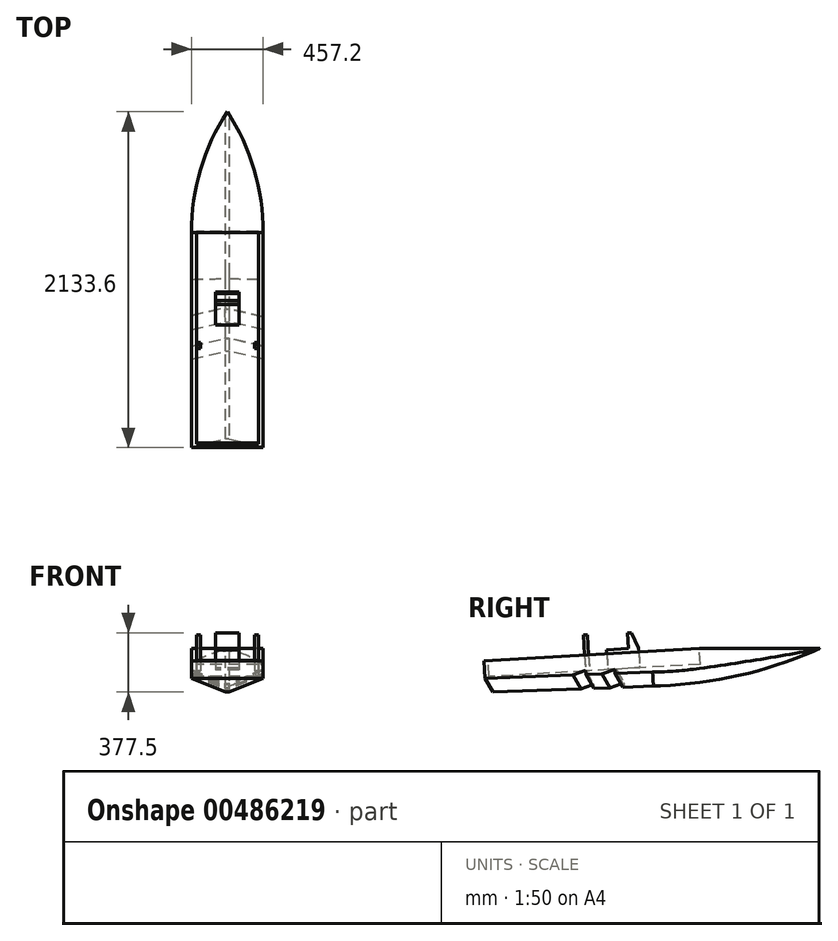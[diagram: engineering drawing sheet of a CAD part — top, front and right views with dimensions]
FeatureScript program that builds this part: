
annotation { "Feature Type Name" : "Feature", "Feature Type Description" : "" }
export const myFeature = defineFeature(function(context is Context, id is Id, definition is map)
    precondition{}
    {
        {
            var Q0;
            Q0=qCreatedBy(makeId("Right.planeOp"),FACE);
            var sketch = newSketch(context, id + "F0", { "sketchPlane" : qUnion([Q0])});
            skLineSegment(sketch, "E0", {"start": v(-869.62, -245.55) * mm, "end": v(497.03, -166) * mm});
            skLineSegment(sketch, "E1", {"start": v(-869.62, -245.55) * mm, "end": v(-863.13, -357.05) * mm});
            skLineSegment(sketch, "E2", {"start": v(-863.13, -357.05) * mm, "end": v(250.24, -314.95) * mm});
            skLineSegment(sketch, "E3", {"start": v(497.03, -166) * mm, "end": v(1263.98, -166) * mm});
            skArc(sketch, "E4", {"start": v(250.24, -314.95) * mm, "mid": v(761.14, -267.9) * mm, "end": v(1263.98, -166) * mm});
            skLineSegment(sketch, "E5", {"start": v(-857.96, -445.8) * mm, "end": v(250.24, -403.9) * mm});
            skArc(sketch, "E6", {"start": v(250.24, -403.9) * mm, "mid": v(768.61, -333.94) * mm, "end": v(1263.98, -166) * mm});
            skLineSegment(sketch, "E7", {"start": v(-863.13, -357.05) * mm, "end": v(-812.8, -444.09) * mm});
            skSolve(sketch);
        }
        {
            var Q0;
            Q0=makeQuery(id+"F0.imprint","IMPRINT",FACE,{"disambiguationData":[TD([[makeQuery(id+"F0.imprint","IMPRINT",EDGE,{"derivedFrom":sQuery(id+"F0.wireOp",EDGE,"E0")}),-1.0]])]});
            var Q1;
            Q1=makeQuery(id+"F0.imprint","IMPRINT",FACE,{"disambiguationData":[TD([[makeQuery(id+"F0.imprint","IMPRINT",EDGE,{"derivedFrom":sQuery(id+"F0.wireOp",EDGE,"E2")}),-1.0]])]});
            extrude(context, id + "F1", {"entities" : qUnion([Q0, Q1]), "depth" : 457.2 * mm, "offsetDistance" : 25.4 * mm});
        }
        {
            var Q0;
            Q0=makeQuery(id+"F1.opExtrude","SWEPT_FACE",FACE,{"disambiguationData":[OSD([sQuery(id+"F0.wireOp",EDGE,"E1")])]});
            var sketch = newSketch(context, id + "F2", { "sketchPlane" : qUnion([Q0])});
            skLineSegment(sketch, "E8", {"start": v(0, -306.29) * mm, "end": v(228.6, -399.45) * mm});
            skPoint(sketch, "E8.endSnap0", {"position": v(228.6, -306.29) * mm});
            skLineSegment(sketch, "E9", {"start": v(228.6, -399.45) * mm, "end": v(457.2, -306.29) * mm});
            skLineSegment(sketch, "E10", {"start": v(457.2, -306.29) * mm, "end": v(500.55, -412.66) * mm});
            skLineSegment(sketch, "E11", {"start": v(500.55, -412.66) * mm, "end": v(-44.86, -412.66) * mm});
            skLineSegment(sketch, "E12", {"start": v(-44.86, -412.66) * mm, "end": v(0, -306.29) * mm});
            skSolve(sketch);
        }
        {
            var Q0;
            Q0=makeQuery(id+"F2.imprint","IMPRINT",FACE,{"disambiguationData":[TD([[makeQuery(id+"F2.imprint","IMPRINT",EDGE,{"derivedFrom":sQuery(id+"F2.wireOp",EDGE,"E8")}),-1.0]])]});
            var Q1;
            Q1=makeQuery(id+"F1.opExtrude","CAP_EDGE",EDGE,{"disambiguationData":[OSD([sQuery(id+"F0.wireOp",EDGE,"E5")])],"isStart":false});
            var Q2;
            Q2=makeQuery(id+"F1.opExtrude","CAP_EDGE",EDGE,{"disambiguationData":[OSD([sQuery(id+"F0.wireOp",EDGE,"E6")])],"isStart":false});
            sweep(context, id + "F3", {"operationType" : NewBodyOperationType.REMOVE, "profiles" : qUnion([Q0]), "path" : qUnion([Q1, Q2])});
        }
        {
            var Q0;
            Q0=makeQuery(id+"F1.opExtrude","SWEPT_FACE",FACE,{"disambiguationData":[OSD([sQuery(id+"F0.wireOp",EDGE,"E3")])]});
            var sketch = newSketch(context, id + "F4", { "sketchPlane" : qUnion([Q0])});
            skPoint(sketch, "E13.startSnap0", {"position": v(228.6, 1263.98) * mm});
            skLineSegment(sketch, "E14", {"start": v(228.6, 1204.03) * mm, "end": v(228.6, 1037.29) * mm, "construction": true});
            skLineSegment(sketch, "E15", {"start": v(0, 497.03) * mm, "end": v(-662.43, 1118.52) * mm});
            skLineSegment(sketch, "E16", {"start": v(-662.43, 1118.52) * mm, "end": v(-136.56, 1315.19) * mm});
            skLineSegment(sketch, "E17", {"start": v(-136.56, 1315.19) * mm, "end": v(782.16, 1315.19) * mm});
            skLineSegment(sketch, "E18", {"start": v(782.16, 1315.19) * mm, "end": v(457.2, 497.03) * mm});
            skArc(sketch, "E19", {"start": v(228.6, 1263.98) * mm, "mid": v(58.37, 897.18) * mm, "end": v(0, 497.03) * mm});
            skArc(sketch, "E20.MirrorCS", {"start": v(228.6, 1263.98) * mm, "mid": v(398.83, 897.18) * mm, "end": v(457.2, 497.03) * mm});
            skSolve(sketch);
        }
        {
            var Q0;
            Q0 = qSketchRegion(id + "F4", true);
            extrude(context, id + "F5", {"entities" : qUnion([Q0]), "operationType" : NewBodyOperationType.REMOVE, "oppositeDirection" : true, "depth" : 584.2 * mm, "offsetDistance" : 25.4 * mm});
        }
        {
            var Q0;
            {var subQ0=sQuery(id+"F0.wireOp",EDGE,"E7");var subQ1=sQuery(id+"F0.wireOp",EDGE,"E3");var subQ2=sQuery(id+"F0.wireOp",EDGE,"E1");var subQ4=sQuery(id+"F0.wireOp",EDGE,"E5");var subQ5=sQuery(id+"F0.wireOp",EDGE,"E0");var subQ6=sQuery(id+"F0.wireOp",EDGE,"E6");Q0=makeQuery(id+"F3.boolean.opBoolean","SPLIT",FACE,{"disambiguationData":[TD([makeQuery(id+"F1.opExtrude","SWEPT_FACE",FACE,{"disambiguationData":[OSD([subQ5])]})])],"derivedFrom":makeQuery(id+"F1.opExtrude","CAP_FACE",FACE,{"disambiguationData":[OSD([subQ5,subQ2,subQ1,subQ4,subQ6,subQ0])],"isStart":true})});}
            var sketch = newSketch(context, id + "F6", { "sketchPlane" : qUnion([Q0])});
            skLineSegment(sketch, "E21", {"start": v(28, -325.47) * mm, "end": v(28.95, -300.1) * mm});
            skLineSegment(sketch, "E22", {"start": v(28.95, -300.1) * mm, "end": v(120.28, -328.96) * mm});
            skLineSegment(sketch, "E23", {"start": v(120.28, -328.96) * mm, "end": v(28, -325.47) * mm});
            skLineSegment(sketch, "E24", {"start": v(224.19, -332.9) * mm, "end": v(224.19, -307.5) * mm});
            skLineSegment(sketch, "E25", {"start": v(224.19, -307.5) * mm, "end": v(306.2, -336) * mm});
            skLineSegment(sketch, "E26", {"start": v(306.2, -336) * mm, "end": v(863.13, -357.05) * mm, "construction": true});
            skSolve(sketch);
        }
        {
            var Q0;
            Q0=makeQuery(id+"F6.imprint","IMPRINT",FACE,{"disambiguationData":[TD([[makeQuery(id+"F6.imprint","IMPRINT",EDGE,{"derivedFrom":sQuery(id+"F6.wireOp",EDGE,"E21")}),-1.0]])]});
            var Q1;
            {var subQ0=sQuery(id+"F6.wireOp",EDGE,"E24");Q1=makeQuery(id+"F6.imprint","IMPRINT",FACE,{"disambiguationData":[TD([[makeQuery(id+"F6.imprint","IMPRINT",EDGE,{"derivedFrom":subQ0}),-1.0]])]});}
            var Q2;
            Q2=makeQuery(id+"F3.boolean.opBoolean","INTERSECT",EDGE,{"derivedFrom":[makeQuery(id+"F1.opExtrude","SWEPT_FACE",FACE,{"disambiguationData":[OSD([sQuery(id+"F0.wireOp",EDGE,"E7")])]}),makeQuery(id+"F3.opSweep","SWEPT_FACE",FACE,{"disambiguationData":[OSD([sQuery(id+"F0.wireOp",EDGE,"E5"),sQuery(id+"F2.wireOp",EDGE,"E8")])]})]});
            sweep(context, id + "F7", {"operationType" : NewBodyOperationType.REMOVE, "profiles" : qUnion([Q0, Q1]), "path" : qUnion([Q2])});
        }
        {
            var Q0;
            {var subQ0=sQuery(id+"F0.wireOp",EDGE,"E7");var subQ1=sQuery(id+"F0.wireOp",EDGE,"E3");var subQ3=sQuery(id+"F0.wireOp",EDGE,"E5");var subQ4=sQuery(id+"F0.wireOp",EDGE,"E1");var subQ5=sQuery(id+"F0.wireOp",EDGE,"E0");var subQ6=sQuery(id+"F0.wireOp",EDGE,"E6");Q0=makeQuery(id+"F3.boolean.opBoolean","SPLIT",FACE,{"disambiguationData":[TD([makeQuery(id+"F1.opExtrude","SWEPT_FACE",FACE,{"disambiguationData":[OSD([subQ5])]})])],"derivedFrom":makeQuery(id+"F1.opExtrude","CAP_FACE",FACE,{"disambiguationData":[OSD([subQ5,subQ4,subQ1,subQ3,subQ6,subQ0])],"isStart":false})});}
            var sketch = newSketch(context, id + "F8", { "sketchPlane" : qUnion([Q0])});
            skLineSegment(sketch, "E27", {"start": v(-863.13, -357.05) * mm, "end": v(-306.2, -336) * mm, "construction": true});
            skLineSegment(sketch, "E28", {"start": v(-306.2, -336) * mm, "end": v(-224.19, -332.9) * mm, "construction": true});
            skLineSegment(sketch, "E29", {"start": v(-224.19, -332.9) * mm, "end": v(-225.66, -307.53) * mm});
            skLineSegment(sketch, "E30", {"start": v(-225.66, -307.53) * mm, "end": v(-306.2, -336) * mm});
            skLineSegment(sketch, "E31", {"start": v(-224.19, -332.9) * mm, "end": v(-120.28, -328.96) * mm, "construction": true});
            skLineSegment(sketch, "E32", {"start": v(-120.28, -328.96) * mm, "end": v(-38.27, -325.86) * mm, "construction": true});
            skLineSegment(sketch, "E33", {"start": v(-38.27, -325.86) * mm, "end": v(-39.74, -300.5) * mm});
            skLineSegment(sketch, "E34", {"start": v(-39.74, -300.5) * mm, "end": v(-120.28, -328.96) * mm});
            skSolve(sketch);
        }
        {
            var Q0;
            {var subQ0=sQuery(id+"F8.wireOp",EDGE,"E29");Q0=makeQuery(id+"F8.imprint","IMPRINT",FACE,{"disambiguationData":[TD([[makeQuery(id+"F8.imprint","IMPRINT",EDGE,{"derivedFrom":subQ0}),1.0]])]});}
            var Q1;
            {var subQ0=sQuery(id+"F8.wireOp",EDGE,"E33");Q1=makeQuery(id+"F8.imprint","IMPRINT",FACE,{"disambiguationData":[TD([[makeQuery(id+"F8.imprint","IMPRINT",EDGE,{"derivedFrom":subQ0}),1.0]])]});}
            var Q2;
            Q2=makeQuery(id+"F3.boolean.opBoolean","INTERSECT",EDGE,{"derivedFrom":[makeQuery(id+"F1.opExtrude","SWEPT_FACE",FACE,{"disambiguationData":[OSD([sQuery(id+"F0.wireOp",EDGE,"E7")])]}),makeQuery(id+"F3.opSweep","SWEPT_FACE",FACE,{"disambiguationData":[OSD([sQuery(id+"F0.wireOp",EDGE,"E5"),sQuery(id+"F2.wireOp",EDGE,"E9")])]})]});
            sweep(context, id + "F9", {"operationType" : NewBodyOperationType.REMOVE, "profiles" : qUnion([Q0, Q1]), "path" : qUnion([Q2])});
        }
        {
            var Q0;
            Q0=makeQuery(id+"F9.boolean.opBoolean","COPY",FACE,{"derivedFrom":makeQuery(id+"F9.opSweep","CAP_FACE",FACE,{"disambiguationData":[OSD([sQuery(id+"F0.wireOp",EDGE,"E1"),sQuery(id+"F0.wireOp",EDGE,"E2"),sQuery(id+"F0.wireOp",EDGE,"E5"),sQuery(id+"F0.wireOp",EDGE,"E7"),sQuery(id+"F2.wireOp",EDGE,"E9"),sQuery(id+"F2.wireOp",EDGE,"E10"),sQuery(id+"F8.wireOp",EDGE,"E29"),sQuery(id+"F8.wireOp",EDGE,"E30")])],"isStart":false})});
            var sketch = newSketch(context, id + "F10", { "sketchPlane" : qUnion([Q0])});
            skLineSegment(sketch, "E35", {"start": v(-255.86, -423.03) * mm, "end": v(-175.33, -394.58) * mm});
            skLineSegment(sketch, "E36", {"start": v(-175.33, -394.58) * mm, "end": v(-173.86, -419.93) * mm});
            skLineSegment(sketch, "E37", {"start": v(-173.86, -419.93) * mm, "end": v(-255.86, -423.03) * mm});
            skSolve(sketch);
        }
        {
            var Q0;
            Q0 = qSketchRegion(id + "F10", true);
            extrude(context, id + "F11", {"entities" : qUnion([Q0]), "operationType" : NewBodyOperationType.REMOVE, "oppositeDirection" : true, "depth" : 25.4 * mm, "offsetDistance" : 25.4 * mm});
        }
        {
            var Q0;
            Q0=makeQuery(id+"F9.boolean.opBoolean","COPY",FACE,{"derivedFrom":makeQuery(id+"F9.opSweep","CAP_FACE",FACE,{"disambiguationData":[OSD([sQuery(id+"F0.wireOp",EDGE,"E1"),sQuery(id+"F0.wireOp",EDGE,"E2"),sQuery(id+"F0.wireOp",EDGE,"E5"),sQuery(id+"F0.wireOp",EDGE,"E7"),sQuery(id+"F2.wireOp",EDGE,"E9"),sQuery(id+"F2.wireOp",EDGE,"E10"),sQuery(id+"F8.wireOp",EDGE,"E33"),sQuery(id+"F8.wireOp",EDGE,"E34")])],"isStart":false})});
            var sketch = newSketch(context, id + "F12", { "sketchPlane" : qUnion([Q0])});
            skLineSegment(sketch, "E38", {"start": v(-69.94, -416) * mm, "end": v(10.59, -387.55) * mm});
            skLineSegment(sketch, "E39", {"start": v(10.59, -387.55) * mm, "end": v(12.07, -412.9) * mm});
            skLineSegment(sketch, "E40", {"start": v(12.07, -412.9) * mm, "end": v(-69.94, -416) * mm});
            skSolve(sketch);
        }
        {
            var Q0;
            Q0 = qSketchRegion(id + "F12", true);
            extrude(context, id + "F13", {"entities" : qUnion([Q0]), "operationType" : NewBodyOperationType.REMOVE, "oppositeDirection" : true, "depth" : 25.4 * mm, "offsetDistance" : 25.4 * mm});
        }
        {
            var Q0;
            Q0=makeQuery(id+"F1.opExtrude","SWEPT_FACE",FACE,{"disambiguationData":[OSD([sQuery(id+"F0.wireOp",EDGE,"E0")])]});
            var sketch = newSketch(context, id + "F14", { "sketchPlane" : qUnion([Q0])});
            skLineSegment(sketch, "E41", {"start": v(0, 486.54) * mm, "end": v(6.35, 486.54) * mm, "construction": true});
            skLineSegment(sketch, "E42", {"start": v(6.35, 486.54) * mm, "end": v(31.75, 486.54) * mm, "construction": true});
            skLineSegment(sketch, "E43", {"start": v(31.75, 486.54) * mm, "end": v(31.75, -882.42) * mm});
            skPoint(sketch, "E43.endSnap0", {"position": v(228.6, -882.42) * mm});
            skLineSegment(sketch, "E44", {"start": v(228.6, 486.54) * mm, "end": v(228.6, 92.47) * mm, "construction": true});
            skLineSegment(sketch, "E45.MirrorCS", {"start": v(425.45, 486.54) * mm, "end": v(425.45, -882.42) * mm});
            skLineSegment(sketch, "E46", {"start": v(228.6, -882.42) * mm, "end": v(228.6, -857.02) * mm, "construction": true});
            skLineSegment(sketch, "E47", {"start": v(228.6, -857.02) * mm, "end": v(425.45, -857.02) * mm});
            skLineSegment(sketch, "E48", {"start": v(425.45, -857.02) * mm, "end": v(31.75, -857.02) * mm});
            skSolve(sketch);
        }
        {
            var Q0;
            {var subQ0=sQuery(id+"F14.wireOp",EDGE,"E47");Q0=makeQuery(id+"F14.imprint","IMPRINT",FACE,{"disambiguationData":[TD([[makeQuery(id+"F14.imprint","IMPRINT",EDGE,{"derivedFrom":subQ0}),1.0]])]});}
            extrude(context, id + "F15", {"entities" : qUnion([Q0]), "operationType" : NewBodyOperationType.REMOVE, "oppositeDirection" : true, "depth" : 101.6 * mm, "offsetDistance" : 25.4 * mm});
        }
        {
            var Q0;
            Q0=makeQuery(id+"F15.boolean.opBoolean","COPY",FACE,{"derivedFrom":makeQuery(id+"F15.opExtrude","CAP_FACE",FACE,{"disambiguationData":[OSD([sQuery(id+"F0.wireOp",EDGE,"E0"),sQuery(id+"F0.wireOp",EDGE,"E3"),sQuery(id+"F14.wireOp",EDGE,"E43"),sQuery(id+"F14.wireOp",EDGE,"E45.MirrorCS"),sQuery(id+"F14.wireOp",EDGE,"E47"),sQuery(id+"F14.wireOp",EDGE,"E48")])],"isStart":false})});
            var sketch = newSketch(context, id + "F16", { "sketchPlane" : qUnion([Q0])});
            skLineSegment(sketch, "E49", {"start": v(228.6, 486.54) * mm, "end": v(228.6, -857.02) * mm, "construction": true});
            skLineSegment(sketch, "E50.bottom", {"start": v(304.8, 101.6) * mm, "end": v(152.4, 101.6) * mm});
            skLineSegment(sketch, "E50.top", {"start": v(304.8, -101.6) * mm, "end": v(152.4, -101.6) * mm});
            skLineSegment(sketch, "E50.left", {"start": v(304.8, 101.6) * mm, "end": v(304.8, -101.6) * mm});
            skLineSegment(sketch, "E50.right", {"start": v(152.4, 101.6) * mm, "end": v(152.4, -101.6) * mm});
            skPoint(sketch, "E50.middle", {"position": v(228.6, 0) * mm});
            skLineSegment(sketch, "E51", {"start": v(31.75, -218.44) * mm, "end": v(57.15, -218.44) * mm});
            skLineSegment(sketch, "E52", {"start": v(57.15, -218.44) * mm, "end": v(57.15, -243.84) * mm});
            skLineSegment(sketch, "E53", {"start": v(57.15, -243.84) * mm, "end": v(31.75, -243.84) * mm});
            skLineSegment(sketch, "E54", {"start": v(31.75, -243.84) * mm, "end": v(57.15, -231.14) * mm, "construction": true});
            skLineSegment(sketch, "E55.MirrorCS", {"start": v(425.45, -218.44) * mm, "end": v(400.05, -218.44) * mm});
            skLineSegment(sketch, "E56.MirrorCS", {"start": v(400.05, -243.84) * mm, "end": v(425.45, -243.84) * mm});
            skLineSegment(sketch, "E57.MirrorCS", {"start": v(400.05, -218.44) * mm, "end": v(400.05, -243.84) * mm});
            skLineSegment(sketch, "E58", {"start": v(31.75, -218.44) * mm, "end": v(31.75, -243.84) * mm});
            skLineSegment(sketch, "E59", {"start": v(434.33, -218.44) * mm, "end": v(425.45, -218.44) * mm});
            skLineSegment(sketch, "E60", {"start": v(425.45, -243.84) * mm, "end": v(425.45, -218.44) * mm});
            skSolve(sketch);
        }
        {
            var Q0;
            Q0 = qSketchRegion(id + "F16", true);
            extrude(context, id + "F17", {"entities" : qUnion([Q0]), "operationType" : NewBodyOperationType.ADD, "depth" : 127 * mm, "offsetDistance" : 25.4 * mm});
        }
        {
            var Q0;
            Q0=makeQuery(id+"F17.opExtrude","SWEPT_FACE",FACE,{"disambiguationData":[OSD([sQuery(id+"F16.wireOp",EDGE,"E50.right")])]});
            var sketch = newSketch(context, id + "F18", { "sketchPlane" : qUnion([Q0])});
            skLineSegment(sketch, "E61", {"start": v(-111.26, -163.01) * mm, "end": v(-66.6, -66.59) * mm});
            skLineSegment(sketch, "E62", {"start": v(-111.26, -163.01) * mm, "end": v(-57.17, -166.16) * mm});
            skLineSegment(sketch, "E63", {"start": v(-66.6, -66.59) * mm, "end": v(-41.25, -68.06) * mm});
            skLineSegment(sketch, "E64", {"start": v(-41.25, -68.06) * mm, "end": v(-47, -166.75) * mm});
            skLineSegment(sketch, "E65", {"start": v(-111.26, -163.01) * mm, "end": v(-47, -166.75) * mm});
            skSolve(sketch);
        }
        {
            var Q0;
            Q0=makeQuery(id+"F18.imprint","IMPRINT",FACE,{"disambiguationData":[TD([[makeQuery(id+"F18.imprint","IMPRINT",EDGE,{"derivedFrom":sQuery(id+"F18.wireOp",EDGE,"E61")}),-1.0]])]});
            extrude(context, id + "F19", {"entities" : qUnion([Q0]), "operationType" : NewBodyOperationType.ADD, "oppositeDirection" : true, "depth" : 152.4 * mm, "offsetDistance" : 25.4 * mm});
        }
        {
            var Q0;
            Q0=makeQuery(id+"F17.opExtrude","CAP_FACE",FACE,{"disambiguationData":[OSD([sQuery(id+"F16.wireOp",EDGE,"E51"),sQuery(id+"F16.wireOp",EDGE,"E52"),sQuery(id+"F16.wireOp",EDGE,"E53"),sQuery(id+"F16.wireOp",EDGE,"E58")])],"isStart":false});
            var Q1;
            Q1=makeQuery(id+"F17.opExtrude","CAP_FACE",FACE,{"disambiguationData":[OSD([sQuery(id+"F16.wireOp",EDGE,"E55.MirrorCS"),sQuery(id+"F16.wireOp",EDGE,"E56.MirrorCS"),sQuery(id+"F16.wireOp",EDGE,"E57.MirrorCS"),sQuery(id+"F16.wireOp",EDGE,"E60")])],"isStart":false});
            extrude(context, id + "F20", {"entities" : qUnion([Q0, Q1]), "operationType" : NewBodyOperationType.ADD, "depth" : 101.6 * mm, "offsetDistance" : 25.4 * mm});
        }
    });
